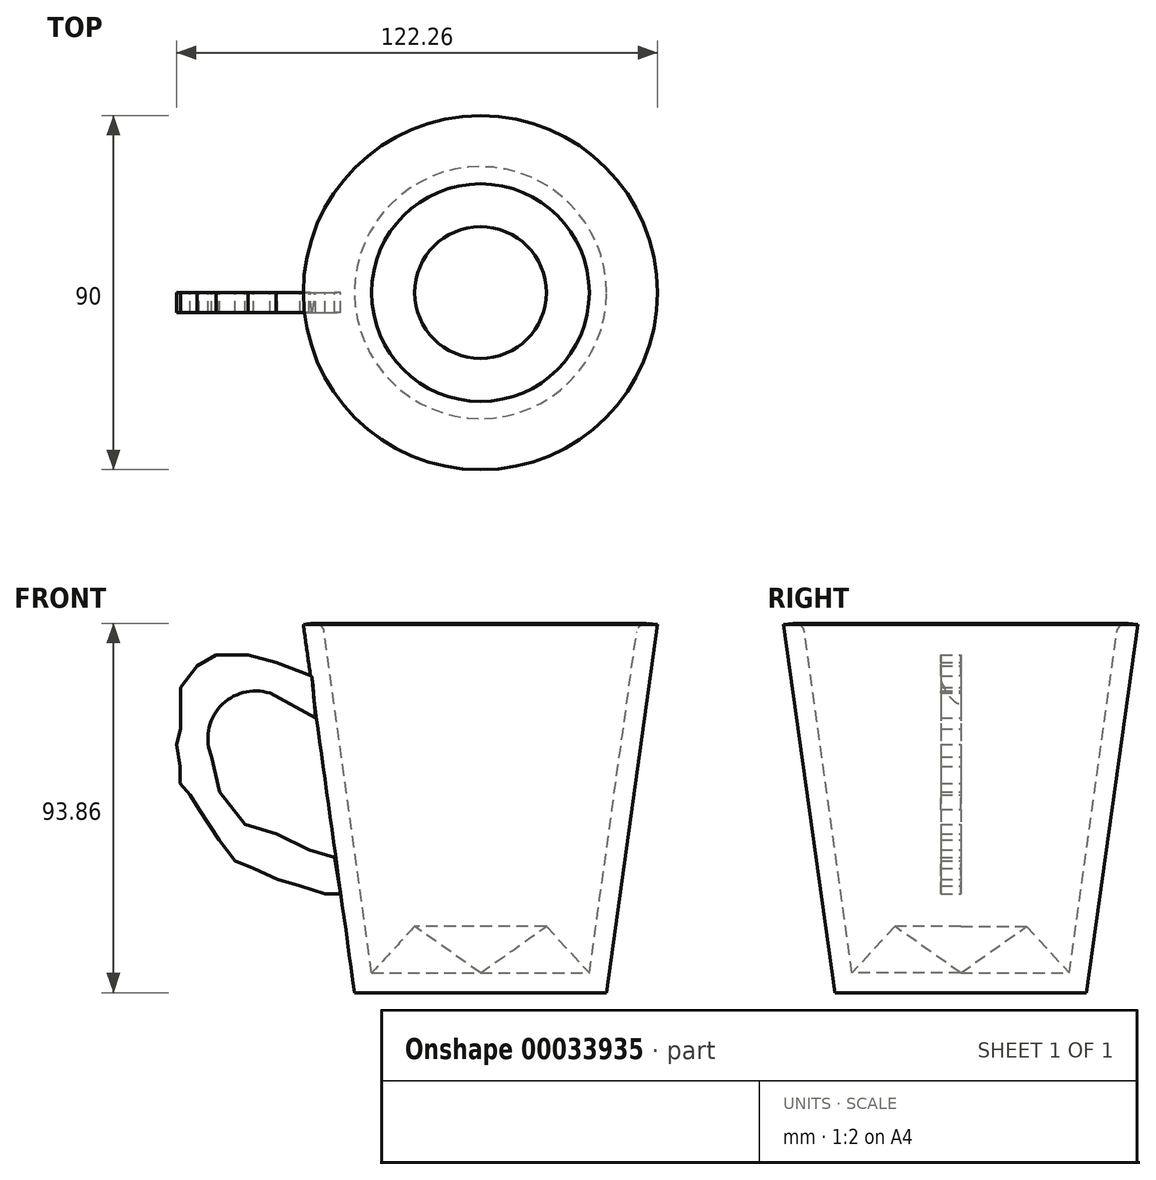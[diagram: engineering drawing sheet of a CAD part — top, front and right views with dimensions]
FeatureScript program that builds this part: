
annotation { "Feature Type Name" : "Feature", "Feature Type Description" : "" }
export const myFeature = defineFeature(function(context is Context, id is Id, definition is map)
    precondition{}
    {
        {
            var Q0;
            Q0=qCreatedBy(makeId("Front.planeOp"),FACE);
            var sketch = newSketch(context, id + "F0", { "sketchPlane" : qUnion([Q0])});
            skLineSegment(sketch, "E0", {"start": v(0, 0) * mm, "end": v(0, 93.5) * mm});
            skLineSegment(sketch, "E1", {"start": v(0, 0) * mm, "end": v(-32, 0) * mm});
            skLineSegment(sketch, "E2", {"start": v(-45, 93.5) * mm, "end": v(-32, 0) * mm});
            skLineSegment(sketch, "E3", {"start": v(-45, 93.5) * mm, "end": v(-40.05, 94.19) * mm});
            skLineSegment(sketch, "E4", {"start": v(-27.65, 5) * mm, "end": v(-40.05, 94.19) * mm});
            skLineSegment(sketch, "E5", {"start": v(-27.65, 5) * mm, "end": v(0, 5) * mm});
            skLineSegment(sketch, "E6", {"start": v(-27.65, 5) * mm, "end": v(-16.73, 16.84) * mm});
            skLineSegment(sketch, "E7", {"start": v(-16.73, 16.84) * mm, "end": v(0, 5) * mm});
            skSolve(sketch);
        }
        {
            var Q0;
            Q0 = qSketchRegion(id + "F0", true);
            var Q1;
            Q1=sQuery(id+"F0.wireOp",EDGE,"E0");
            revolve(context, id + "F1", {"entities" : qUnion([Q0]), "axis" : qUnion([Q1]), "revolveType" : RevolveType.FULL});
        }
        {
            var Q0;
            Q0=qCreatedBy(makeId("Front.planeOp"),FACE);
            var sketch = newSketch(context, id + "F2", { "sketchPlane" : qUnion([Q0])});
            skCircle(sketch, "E8", {"center": v(-57.15, 64.57) * mm, "radius": 12.1 * mm});
            skLineSegment(sketch, "E9", {"start": v(-42.82, 80.39) * mm, "end": v(-51.94, 83.93) * mm});
            skLineSegment(sketch, "E10", {"start": v(-51.94, 83.93) * mm, "end": v(-59.02, 85.79) * mm});
            skLineSegment(sketch, "E11", {"start": v(-59.02, 85.79) * mm, "end": v(-67.2, 85.79) * mm});
            skLineSegment(sketch, "E12", {"start": v(-67.2, 85.79) * mm, "end": v(-72.05, 83) * mm});
            skLineSegment(sketch, "E13", {"start": v(-72.05, 83) * mm, "end": v(-76.14, 77.6) * mm});
            skLineSegment(sketch, "E14", {"start": v(-76.14, 77.6) * mm, "end": v(-76.14, 72.94) * mm});
            skLineSegment(sketch, "E15", {"start": v(-76.14, 72.94) * mm, "end": v(-76.14, 66.99) * mm});
            skLineSegment(sketch, "E16", {"start": v(-76.14, 66.99) * mm, "end": v(-77.26, 63.08) * mm});
            skLineSegment(sketch, "E17", {"start": v(-77.26, 63.08) * mm, "end": v(-76.33, 57.5) * mm});
            skLineSegment(sketch, "E18", {"start": v(-76.33, 57.5) * mm, "end": v(-76.33, 53.2) * mm});
            skLineSegment(sketch, "E19", {"start": v(-76.33, 53.2) * mm, "end": v(-73.72, 50.23) * mm});
            skLineSegment(sketch, "E20", {"start": v(-71.49, 46.5) * mm, "end": v(-73.72, 50.23) * mm});
            skLineSegment(sketch, "E21", {"start": v(-71.49, 46.5) * mm, "end": v(-66.46, 38.87) * mm});
            skLineSegment(sketch, "E22", {"start": v(-66.46, 38.87) * mm, "end": v(-62.37, 33.48) * mm});
            skLineSegment(sketch, "E23", {"start": v(-62.37, 33.48) * mm, "end": v(-57.71, 31.61) * mm});
            skLineSegment(sketch, "E24", {"start": v(-57.71, 31.61) * mm, "end": v(-51.57, 28.82) * mm});
            skLineSegment(sketch, "E25", {"start": v(-51.57, 28.82) * mm, "end": v(-45.8, 27.15) * mm});
            skLineSegment(sketch, "E26", {"start": v(-45.8, 27.15) * mm, "end": v(-39.47, 25.1) * mm});
            skLineSegment(sketch, "E27", {"start": v(-39.47, 25.1) * mm, "end": v(-35.56, 25.1) * mm});
            skLineSegment(sketch, "E28", {"start": v(-68.3, 59.85) * mm, "end": v(-66.28, 50.98) * mm});
            skLineSegment(sketch, "E29", {"start": v(-66.28, 50.98) * mm, "end": v(-59.76, 42.78) * mm});
            skLineSegment(sketch, "E30", {"start": v(-59.76, 42.78) * mm, "end": v(-51.75, 40.36) * mm});
            skLineSegment(sketch, "E31", {"start": v(-51.75, 40.36) * mm, "end": v(-43.56, 36.27) * mm});
            skLineSegment(sketch, "E32", {"start": v(-43.56, 36.27) * mm, "end": v(-37.05, 34.4) * mm});
            skLineSegment(sketch, "E33", {"start": v(-53.5, 76.1) * mm, "end": v(-41.89, 69.78) * mm});
            skLineSegment(sketch, "E34", {"start": v(-35.56, 25.1) * mm, "end": v(-37.05, 34.4) * mm});
            skLineSegment(sketch, "E35", {"start": v(-42.82, 80.39) * mm, "end": v(-41.89, 69.78) * mm});
            skSolve(sketch);
        }
        {
            var Q0;
            Q0=makeQuery(id+"F2.imprint","IMPRINT",FACE,{"disambiguationData":[TD([[makeQuery(id+"F2.imprint","IMPRINT",EDGE,{"derivedFrom":sQuery(id+"F2.wireOp",EDGE,"E9")}),1.0]])]});
            var Q1;
            {var subQ0=sQuery(id+"F2.wireOp",EDGE,"E33");var subQ1=sQuery(id+"F2.wireOp",EDGE,"E8");var subQ3=makeQuery(id+"F2.imprint","INTERSECT",VERTEX,{"disambiguationData":[OD(0.0)],"derivedFrom":[subQ1,subQ0]});Q1=makeQuery(id+"F2.imprint","IMPRINT",FACE,{"disambiguationData":[TD([[makeQuery(id+"F2.imprint","IMPRINT",EDGE,{"disambiguationData":[TD([[subQ3,1.0]])],"derivedFrom":subQ1}),1.0]])]});}
            extrude(context, id + "F3", {"entities" : qUnion([Q0, Q1]), "operationType" : NewBodyOperationType.ADD, "depth" : 5.08 * mm});
        }
        {
            var Q0;
            Q0=makeQuery(id+"F1.opRevolve","SWEPT_EDGE",EDGE,{"disambiguationData":[OSD([sQuery(id+"F0.wireOp",EDGE,"E3"),sQuery(id+"F0.wireOp",EDGE,"E4")])]});
            fillet(context, id + "F4", {"entities" : qUnion([Q0]), "radius" : 2.54 * mm, "tangentPropagation" : true, "allowEdgeOverflow" : false});
        }
    });
